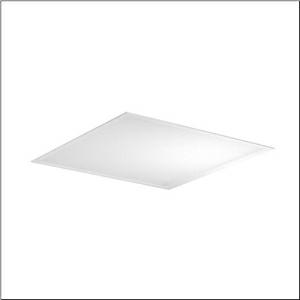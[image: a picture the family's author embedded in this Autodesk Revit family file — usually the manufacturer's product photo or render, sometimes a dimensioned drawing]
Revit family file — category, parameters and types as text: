
# Revit family: apollon_r__31_square_51mp12wd2m42_b676
name_source: partatom
category: Lighting Fixtures
units: mm (PartAtom-declared; Revit-internal decimal feet)

## family parameters
Cut with Voids When Loaded = No
Host = Face
Light Source = No
Part Type = Normal
Room Calculation Point = No
Round Connector Dimension = Use Diameter
Shared = No

## types (1)
- --- (1 x LED, 4000 lm, 27.5 W, 4000K)
    Apparent Load = 28 VA
    CIE Flux Codes = 62 87 97 100 100
    Color Rendering = 80
    Color Temperature = 4000K
    Default Elevation = 1800 mm
    Description = Apollon® 31 square, office luminaire, primary optical cover: micro prismatic cover, of PMMA, CAT 2 (L<= 3000cd/m²), light emission: direct distribution, primary light characteristic: symmetric, installation type: lay-in mounting, LED, rated luminous flux: 4.000lm, luminous efficacy: 142lm/W, light colour: 830/840, colour temperature: 3000/4000K, control gear: DALI 2, Multilumen, with terminal, 5-pole, mains connection: 220..240V, AC/DC, 0/50..60Hz, rated input power: 28W, suitable for self-contained emergency lighting element 58DB00B013A with integrated self-test function according to EN 60598-2-22, housing, of aluminium, traffic white (RAL 9016), module: M600, length: 595mm, width: 595mm, height: 62mm, recess depth: 180mm, housing upper side, of sheet steel, coated, protection rating (complete): IP20, protection rating (on room side): IP40, insulation class (complete): insulation class II (safety insulation), certification: CE, ENEC, impact resistance: IK03, permissible operating ambient temperature: -20..+40°C, permissible storage temperature: -20..+60°C, standard: EN 60598-2-22, packaging unit: 1 piece
    Height = 0 mm  [stored 0 ft]
    Lamp = 1 x LED
    Lamp Light Flux = 4000 lm
    Lamp Power = 27.5 W
    Lamp count = 1
    Length = 595 mm
    Luminous efficacy = 145 lm/W
    Manufacturer = Siteco
    ModVariant = No
    Model = 51MP12WD2M42
    Mounting Place = Ceiling
    Mounting Type = Recessed
    Number of Poles = 1
    OnlyDefault = Yes
    Power Factor = 1
    Product Name = Apollon® 31 square
    Product group = office luminaire | ceiling recessed
    ProductGroupID = 400
    Protection Class = Protection class II
    Protection Degree = IP 20
    RLX_Detail_Level = 1
    RLX_Emergency_Light_Flux = 0 lm
    RLX_Emergency_Type = 0
    RLX_Emergency_Type_DB = No
    RlxData = <blob elided: 12977 chars, md5=d8421245>
    Socket = socket
    Standby Power = 0 W
    System Light Flux = 4000 lm
    System Power = 28 W
    Type Comments = factory setting: colour temperature 4000K
    Type Image = l_1291035.jpg
    URL = http://relux.com
    VarID = @adj_098141
    Voltage = 0 V
    Weight = 0.00 kg
    Width = 595 mm

note: [stored X ft] marks values corroborated as IEEE doubles in the binary element streams (Revit-internal decimal feet)

## geometry (parser evidence)
native form markers: Sweep x9
no freeform markers — native parametric forms only
